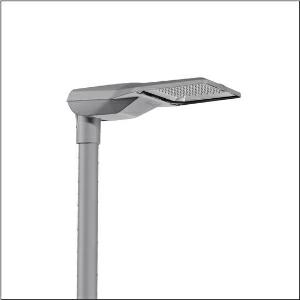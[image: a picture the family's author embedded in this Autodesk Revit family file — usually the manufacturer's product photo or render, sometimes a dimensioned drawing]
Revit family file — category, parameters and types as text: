
# Revit family: streetlight_sl_21_iq_midi___st1_0a_5xe3d41d08nb_8ddf
name_source: partatom
category: Lighting Fixtures
units: mm (PartAtom-declared; Revit-internal decimal feet)

## family parameters
Cut with Voids When Loaded = No
Host = Face
Light Source = No
Part Type = Normal
Room Calculation Point = No
Round Connector Dimension = Use Diameter
Shared = No

## types (1)
- --- (1 x LED, 24250 lm, 155.5 W, 4000K)
    Apparent Load = 155 VA
    CIE Flux Codes = 40 73 97 100 100
    Color Rendering = 70
    Color Temperature = 4000K
    Default Elevation = 1800 mm
    Description = Streetlight SL 21 iQ midi, mast luminaire, primary light control with lens, of PMMA, primary optical cover: cover, of toughened safety glass, transparent, light distribution: ST1.0a, light emission: direct distribution, primary light characteristic: asymmetric, installation type: post-top, side-entry, LED, High Power LED, rated luminous flux: 24.250lm, luminous efficacy: 156lm/W, light colour: 740, colour temperature: 4000K, control: Auto-Match, Temp-Guard, Lumen-Switch, Night-Set, Smart-Wire, Light-Fading, Desk-Remote (wireless, voltage-free reading and setting of iQ features in the workshop via application-optimized NFC function/RFID function), optimised constant luminous flux control (CLO 2.0), presetting dimming linear, mains connection: 230..240V, AC, 50/60Hz, start of lifetime: 156W, end of service life: 162W, reduction: 69W, luminaire housing, of diecast aluminium, powder-coated, Siteco® metallic grey (DB 702S), corrosivity category C5 mid according to DIN EN ISO 12944, please order mast flange separately, inclination adjustable: 0°, 5°, 10°, 15°, sealing non-destructively replaceable, multi-level sealing system, length: 644mm, width: 335mm, height: 110mm, mast flange for spigot size: 42mm (side-entry): 5XC10008XM4, 60/48mm (side-entry/post-top): 5XC10108XM2, 76/60mm (side-entry/post-top): 5XC10108XM1, protection rating (complete): IP66, insulation class (complete): insulation class II (safety insulation), certification: CE, ENEC, ENEC+, VDE, impact resistance: IK09, permissible operating ambient temperature for outdoor applications: -40..+50°C, standard-compliant lighting for roads and squares, packaging unit: 1 piece

Light Distribution: ST1.0a
    Height = 111 mm
    Lamp = 1 x LED
    Lamp Light Flux = 24250 lm
    Lamp Power = 155.5 W
    Lamp count = 1
    Length = 644 mm
    Luminous efficacy = 156 lm/W
    Manufacturer = Siteco
    ModVariant = No
    Model = 5XE3D41D08NB
    Number of Poles = 1
    OnlyDefault = Yes
    Power Factor = 1
    Product Name = Streetlight SL 21 iQ midi | ST1.0a
    Product group = mast luminaire | pylon top
    ProductGroupID = 6100
    Protection Class = Protection class II
    Protection Degree = IP 66
    RLX_Detail_Level = 1
    RLX_Emergency_Light_Flux = 0 lm
    RLX_Emergency_Type = 0
    RLX_Emergency_Type_DB = No
    RlxData = <blob elided: 91169 chars, md5=145477b6>
    Socket = socket
    Standby Power = 0 W
    System Light Flux = 24250 lm
    System Power = 155 W
    Type Comments = factory setting: luminous flux: 100 % | dim-lin: 254 | 823 mA
    Type Image = l_1004298.jpg
    URL = http://relux.com
    VarID = @adj_103543
    Voltage = 0 V
    Weight = 0.00 kg
    Width = 336 mm

## geometry (parser evidence)
native form markers: Blend x4, Sweep x11
no freeform markers — native parametric forms only
